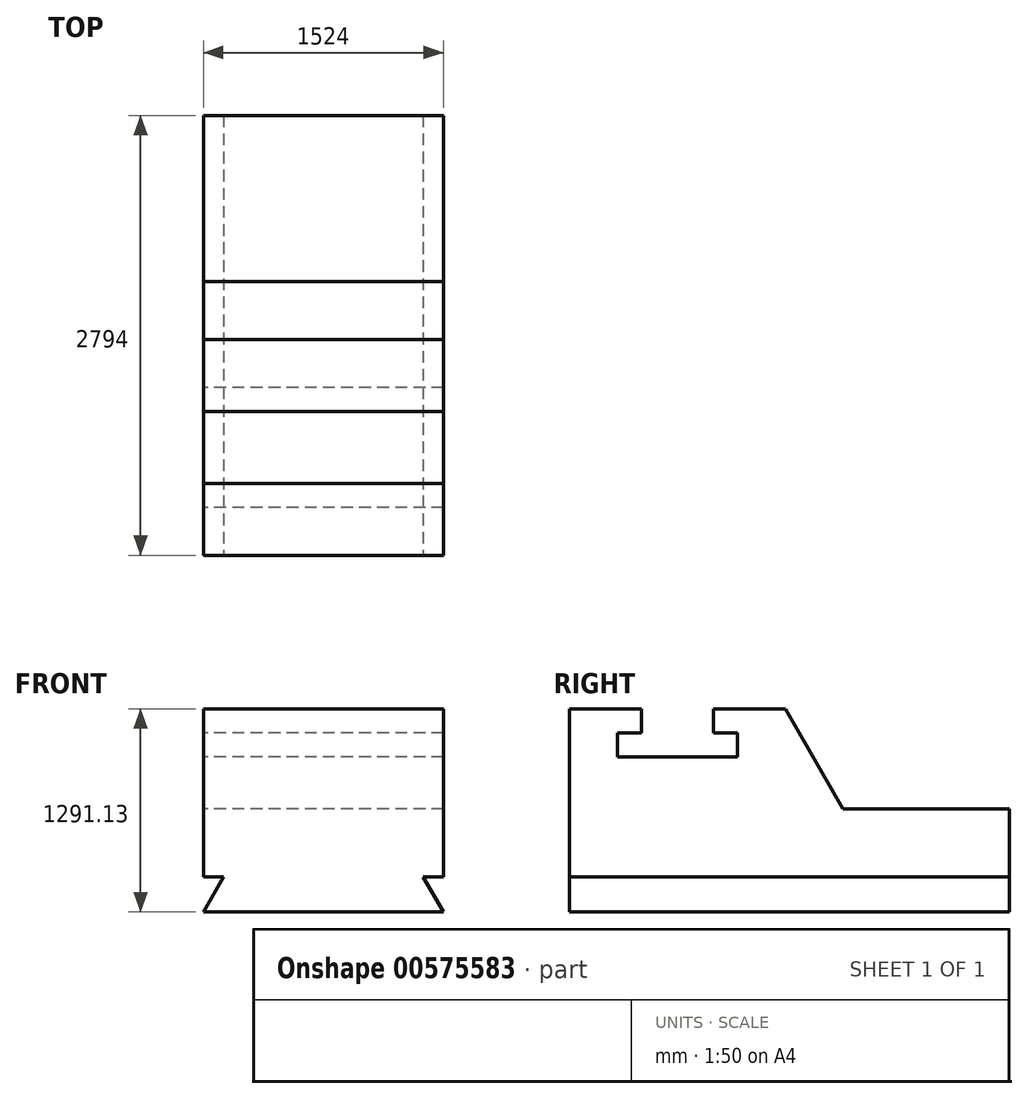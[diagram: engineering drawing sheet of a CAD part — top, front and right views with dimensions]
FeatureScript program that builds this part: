
annotation { "Feature Type Name" : "Feature", "Feature Type Description" : "" }
export const myFeature = defineFeature(function(context is Context, id is Id, definition is map)
    precondition{}
    {
        {
            var Q0;
            Q0=qCreatedBy(makeId("Right.planeOp"),FACE);
            var sketch = newSketch(context, id + "F0", { "sketchPlane" : qUnion([Q0])});
            skLineSegment(sketch, "E0", {"start": v(2586.84, -61.53) * mm, "end": v(-207.16, -61.53) * mm});
            skLineSegment(sketch, "E1", {"start": v(-207.16, -61.53) * mm, "end": v(-207.16, 1005.27) * mm});
            skLineSegment(sketch, "E2", {"start": v(-207.16, 1005.27) * mm, "end": v(250.04, 1005.27) * mm});
            skLineSegment(sketch, "E3", {"start": v(250.04, 1005.27) * mm, "end": v(250.04, 852.87) * mm});
            skLineSegment(sketch, "E4", {"start": v(250.04, 852.87) * mm, "end": v(97.64, 852.87) * mm});
            skLineSegment(sketch, "E5", {"start": v(97.64, 852.87) * mm, "end": v(97.64, 700.47) * mm});
            skLineSegment(sketch, "E6", {"start": v(97.64, 700.47) * mm, "end": v(859.64, 700.47) * mm});
            skLineSegment(sketch, "E7", {"start": v(859.64, 700.47) * mm, "end": v(859.64, 852.87) * mm});
            skLineSegment(sketch, "E8", {"start": v(859.64, 852.87) * mm, "end": v(707.24, 852.87) * mm});
            skLineSegment(sketch, "E9", {"start": v(707.24, 852.87) * mm, "end": v(707.24, 1005.27) * mm});
            skLineSegment(sketch, "E10", {"start": v(707.24, 1005.27) * mm, "end": v(1164.44, 1005.27) * mm});
            skLineSegment(sketch, "E11", {"start": v(2586.84, -61.53) * mm, "end": v(2586.84, 370.27) * mm});
            skLineSegment(sketch, "E12", {"start": v(1532.13, 368.41) * mm, "end": v(1164.44, 1005.27) * mm});
            skLineSegment(sketch, "E13", {"start": v(1532.13, 368.41) * mm, "end": v(2586.84, 370.27) * mm});
            skSolve(sketch);
        }
        {
            var Q0;
            Q0=makeQuery(id+"F0.imprint","IMPRINT",FACE,{"disambiguationData":[TD([[makeQuery(id+"F0.imprint","IMPRINT",EDGE,{"derivedFrom":sQuery(id+"F0.wireOp",EDGE,"E0")}),-1.0]])]});
            extrude(context, id + "F1", {"entities" : qUnion([Q0]), "depth" : 1524 * mm, "offsetDistance" : 25.4 * mm});
        }
        {
            var Q0;
            Q0=makeQuery(id+"F1.opExtrude","SWEPT_FACE",FACE,{"disambiguationData":[OSD([sQuery(id+"F0.wireOp",EDGE,"E1")])]});
            var sketch = newSketch(context, id + "F2", { "sketchPlane" : qUnion([Q0])});
            skLineSegment(sketch, "E14", {"start": v(1524, -285.86) * mm, "end": v(1394.49, -61.53) * mm});
            skLineSegment(sketch, "E15", {"start": v(1524, -285.86) * mm, "end": v(0, -285.86) * mm});
            skLineSegment(sketch, "E16", {"start": v(0, -285.86) * mm, "end": v(129.51, -61.53) * mm});
            skSolve(sketch);
        }
        {
            var Q0;
            {var subQ0=sQuery(id+"F2.wireOp",EDGE,"E14");Q0=makeQuery(id+"F2.imprint","IMPRINT",FACE,{"disambiguationData":[TD([[makeQuery(id+"F2.imprint","IMPRINT",EDGE,{"derivedFrom":subQ0}),1.0]])]});}
            extrude(context, id + "F3", {"entities" : qUnion([Q0]), "operationType" : NewBodyOperationType.ADD, "oppositeDirection" : true, "depth" : 2794 * mm, "offsetDistance" : 25.4 * mm});
        }
    });
